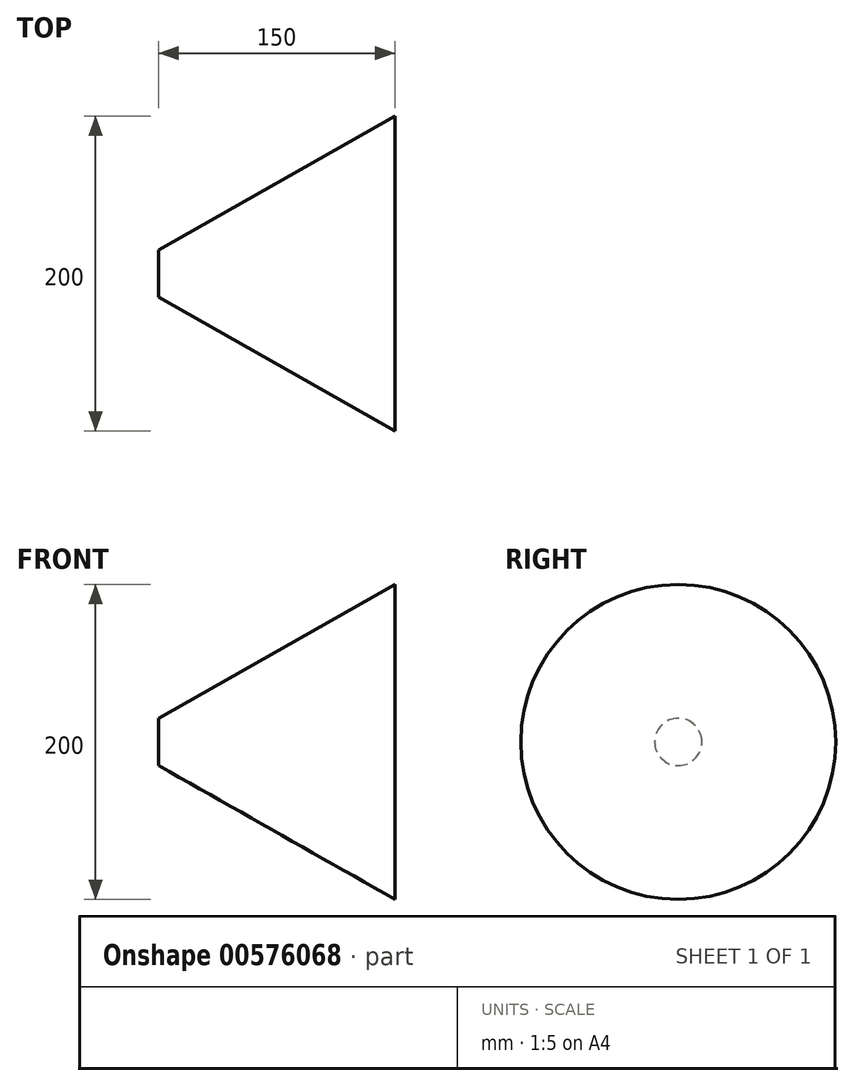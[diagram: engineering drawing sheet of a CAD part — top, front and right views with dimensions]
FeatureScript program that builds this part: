
annotation { "Feature Type Name" : "Feature", "Feature Type Description" : "" }
export const myFeature = defineFeature(function(context is Context, id is Id, definition is map)
    precondition{}
    {
        {
            var Q0;
            Q0=qCreatedBy(makeId("Right.planeOp"),FACE);
            var sketch = newSketch(context, id + "F0", { "sketchPlane" : qUnion([Q0])});
            skCircle(sketch, "E0", {"center": v(0, 0) * mm, "radius": 15 * mm});
            skSolve(sketch);
        }
        {
            var Q0;
            Q0=qCreatedBy(makeId("Right.planeOp"),FACE);
            cPlane(context, id + "F1", {"entities" : qUnion([Q0]), "cplaneType" : CPlaneType.OFFSET, "offset" : 150 * mm, "width" : 150 * mm, "height" : 150 * mm});
        }
        {
            var Q0;
            Q0=qCreatedBy(id+"F1.planeOp",FACE);
            var sketch = newSketch(context, id + "F2", { "sketchPlane" : qUnion([Q0])});
            skCircle(sketch, "E1", {"center": v(0, 0) * mm, "radius": 100 * mm});
            skSolve(sketch);
        }
        {
            var Q0;
            Q0=makeQuery(id+"F2.imprint","IMPRINT",FACE,{"disambiguationData":[TD([[makeQuery(id+"F2.imprint","IMPRINT",EDGE,{"derivedFrom":sQuery(id+"F2.wireOp",EDGE,"E1")}),1.0]])]});
            var Q1;
            Q1=makeQuery(id+"F0.imprint","IMPRINT",FACE,{"disambiguationData":[TD([[makeQuery(id+"F0.imprint","IMPRINT",EDGE,{"derivedFrom":sQuery(id+"F0.wireOp",EDGE,"E0")}),1.0]])]});
            loft(context, id + "F3", {"sheetProfilesArray" : [{ "sheetProfileEntities" : qUnion([Q0]) }, { "sheetProfileEntities" : qUnion([Q1]) }]});
        }
    });
